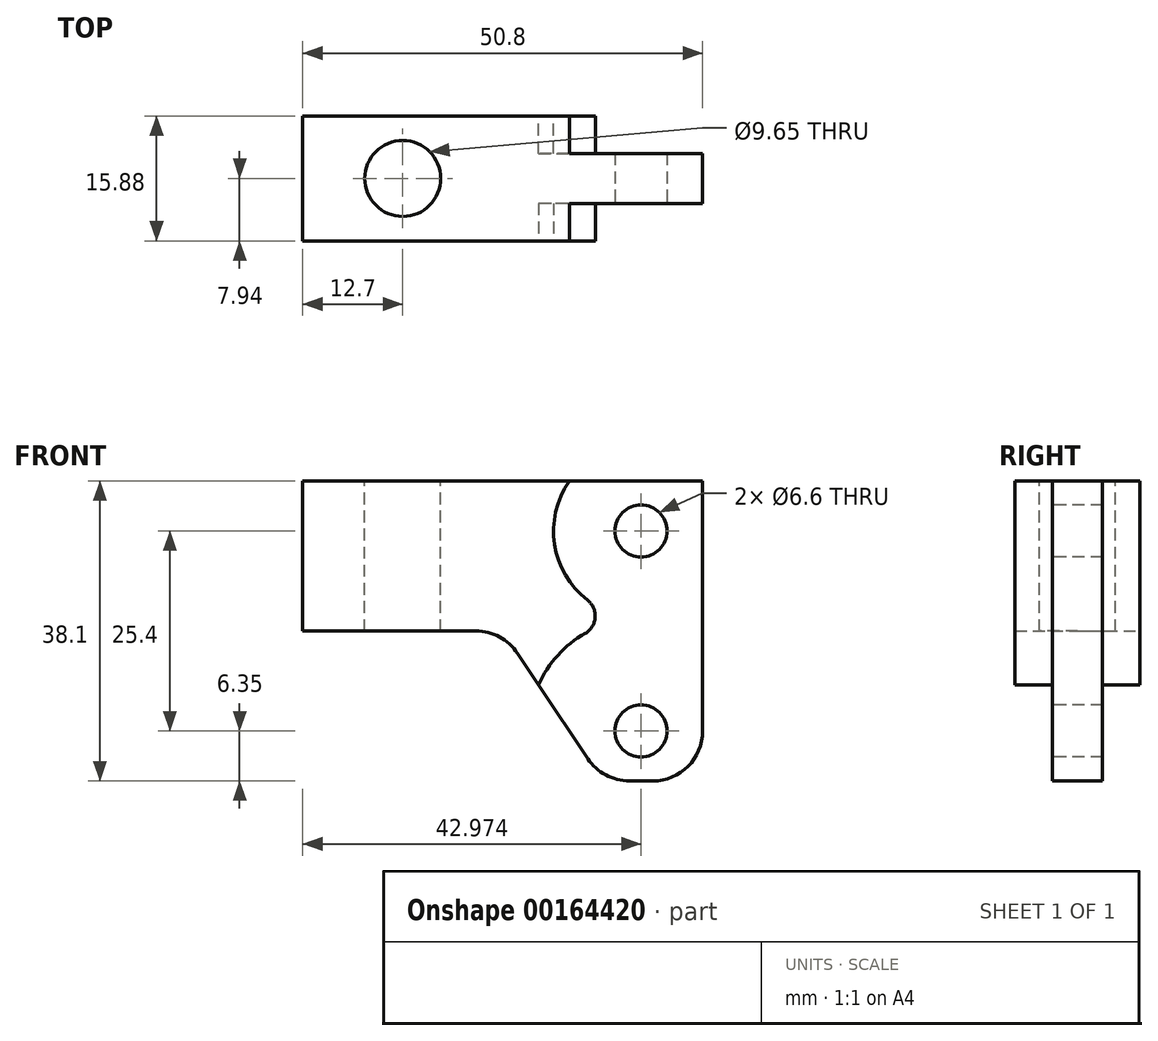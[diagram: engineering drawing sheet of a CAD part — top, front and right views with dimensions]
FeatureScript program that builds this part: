
annotation { "Feature Type Name" : "Feature", "Feature Type Description" : "" }
export const myFeature = defineFeature(function(context is Context, id is Id, definition is map)
    precondition{}
    {
        {
            var Q0;
            Q0=qCreatedBy(makeId("Front.planeOp"),FACE);
            var sketch = newSketch(context, id + "F0", { "sketchPlane" : qUnion([Q0])});
            skLineSegment(sketch, "E0", {"start": v(0, 0) * mm, "end": v(0, 19.05) * mm});
            skLineSegment(sketch, "E1", {"start": v(0, 19.05) * mm, "end": v(50.8, 19.05) * mm});
            skLineSegment(sketch, "E2", {"start": v(50.8, 19.05) * mm, "end": v(50.8, -19.05) * mm});
            skLineSegment(sketch, "E3", {"start": v(50.8, -19.05) * mm, "end": v(38.1, -19.05) * mm});
            skLineSegment(sketch, "E4", {"start": v(38.1, -19.05) * mm, "end": v(25.4, 0) * mm});
            skLineSegment(sketch, "E5", {"start": v(25.4, 0) * mm, "end": v(0, 0) * mm});
            skSolve(sketch);
        }
        {
            var Q0;
            Q0 = qSketchRegion(id + "F0", true);
            extrude(context, id + "F1", {"entities" : qUnion([Q0]), "depth" : 7.94 * mm, "hasSecondDirection" : true, "secondDirectionOppositeDirection" : true, "secondDirectionDepth" : 7.94 * mm});
        }
        {
            var Q0;
            Q0=makeQuery(id+"F1.opExtrude","SWEPT_EDGE",EDGE,{"disambiguationData":[OSD([sQuery(id+"F0.wireOp",EDGE,"E4"),sQuery(id+"F0.wireOp",EDGE,"E5")])]});
            var Q1;
            Q1=makeQuery(id+"F1.opExtrude","SWEPT_EDGE",EDGE,{"disambiguationData":[OSD([sQuery(id+"F0.wireOp",EDGE,"E3"),sQuery(id+"F0.wireOp",EDGE,"E4")])]});
            var Q2;
            Q2=makeQuery(id+"F1.opExtrude","SWEPT_EDGE",EDGE,{"disambiguationData":[OSD([sQuery(id+"F0.wireOp",EDGE,"E2"),sQuery(id+"F0.wireOp",EDGE,"E3")])]});
            fillet(context, id + "F2", {"entities" : qUnion([Q0, Q1, Q2]), "radius" : 6.35 * mm, "tangentPropagation" : true, "allowEdgeOverflow" : false});
        }
        {
            var Q0;
            Q0=makeQuery(id+"F1.opExtrude","CAP_FACE",FACE,{"disambiguationData":[OSD([sQuery(id+"F0.wireOp",EDGE,"E0"),sQuery(id+"F0.wireOp",EDGE,"E1"),sQuery(id+"F0.wireOp",EDGE,"E2"),sQuery(id+"F0.wireOp",EDGE,"E3"),sQuery(id+"F0.wireOp",EDGE,"E4"),sQuery(id+"F0.wireOp",EDGE,"E5")])],"isStart":false});
            var sketch = newSketch(context, id + "F3", { "sketchPlane" : qUnion([Q0])});
            skCircle(sketch, "E6", {"center": v(42.97, -12.7) * mm, "radius": 3.3 * mm});
            skCircle(sketch, "E7", {"center": v(42.97, 12.7) * mm, "radius": 3.3 * mm});
            skLineSegment(sketch, "E8", {"start": v(42.97, 12.7) * mm, "end": v(42.97, -12.7) * mm, "construction": true});
            skLineSegment(sketch, "E9", {"start": v(42.97, -12.7) * mm, "end": v(50.8, -12.7) * mm, "construction": true});
            skLineSegment(sketch, "E10", {"start": v(42.97, 12.7) * mm, "end": v(42.97, 19.05) * mm, "construction": true});
            skLineSegment(sketch, "E11", {"start": v(36.5, -8.94) * mm, "end": v(42.97, -18.65) * mm, "construction": true});
            skLineSegment(sketch, "E12", {"start": v(42.97, -12.7) * mm, "end": v(40.23, -14.53) * mm, "construction": true});
            skLineSegment(sketch, "E13", {"start": v(42.97, -12.7) * mm, "end": v(42.97, -19.05) * mm, "construction": true});
            skSolve(sketch);
        }
        {
            var Q0;
            Q0 = qSketchRegion(id + "F3", true);
            extrude(context, id + "F4", {"entities" : qUnion([Q0]), "operationType" : NewBodyOperationType.REMOVE, "oppositeDirection" : true, "depth" : 25.4 * mm});
        }
        {
            var Q0;
            Q0=makeQuery(id+"F1.opExtrude","CAP_FACE",FACE,{"disambiguationData":[OSD([sQuery(id+"F0.wireOp",EDGE,"E0"),sQuery(id+"F0.wireOp",EDGE,"E1"),sQuery(id+"F0.wireOp",EDGE,"E2"),sQuery(id+"F0.wireOp",EDGE,"E3"),sQuery(id+"F0.wireOp",EDGE,"E4"),sQuery(id+"F0.wireOp",EDGE,"E5")])],"isStart":false});
            var sketch = newSketch(context, id + "F5", { "sketchPlane" : qUnion([Q0])});
            skArc(sketch, "E14", {"start": v(42.97, 1.59) * mm, "mid": v(32.87, -22.8) * mm, "end": v(57.26, -12.7) * mm});
            skArc(sketch, "E15", {"start": v(54.09, 12.7) * mm, "mid": v(35.12, 20.56) * mm, "end": v(42.97, 1.59) * mm});
            skLineSegment(sketch, "E16.bottom", {"start": v(42.97, 12.7) * mm, "end": v(61.7, 12.7) * mm});
            skLineSegment(sketch, "E16.top", {"start": v(42.97, -12.7) * mm, "end": v(61.7, -12.7) * mm});
            skLineSegment(sketch, "E16.left", {"start": v(42.97, 12.7) * mm, "end": v(42.97, -12.7) * mm});
            skLineSegment(sketch, "E16.right", {"start": v(61.7, 12.7) * mm, "end": v(61.7, -12.7) * mm});
            skSolve(sketch);
        }
        {
            var Q0;
            Q0 = qSketchRegion(id + "F5", true);
            extrude(context, id + "F6", {"entities" : qUnion([Q0]), "operationType" : NewBodyOperationType.REMOVE, "oppositeDirection" : true, "depth" : 4.76 * mm});
        }
        {
            var Q0;
            Q0=makeQuery(id+"F6.boolean.opBoolean","COPY",EDGE,{"derivedFrom":makeQuery(id+"F6.opExtrude","SWEPT_EDGE",EDGE,{"disambiguationData":[OSD([sQuery(id+"F5.wireOp",EDGE,"E14"),sQuery(id+"F5.wireOp",EDGE,"E15")])]})});
            fillet(context, id + "F7", {"entities" : qUnion([Q0]), "radius" : 2.54 * mm, "tangentPropagation" : true, "allowEdgeOverflow" : false});
        }
        {
            var Q0;
            Q0=makeQuery(id+"F1.opExtrude","CAP_FACE",FACE,{"disambiguationData":[OSD([sQuery(id+"F0.wireOp",EDGE,"E0"),sQuery(id+"F0.wireOp",EDGE,"E1"),sQuery(id+"F0.wireOp",EDGE,"E2"),sQuery(id+"F0.wireOp",EDGE,"E3"),sQuery(id+"F0.wireOp",EDGE,"E4"),sQuery(id+"F0.wireOp",EDGE,"E5")])],"isStart":true});
            var sketch = newSketch(context, id + "F8", { "sketchPlane" : qUnion([Q0])});
            skArc(sketch, "E17.0", {"start": v(-50.8, -12.7) * mm, "mid": v(-48.94, -17.2) * mm, "end": v(-44.45, -19.05) * mm});
            skLineSegment(sketch, "E17.1", {"start": v(-50.8, 19.05) * mm, "end": v(-50.8, -12.7) * mm});
            skLineSegment(sketch, "E17.2", {"start": v(-44.45, -19.05) * mm, "end": v(-41.5, -19.05) * mm});
            skLineSegment(sketch, "E17.3", {"start": v(-33.85, 19.05) * mm, "end": v(-50.8, 19.05) * mm});
            skArc(sketch, "E17.4", {"start": v(-41.5, -19.05) * mm, "mid": v(-38.5, -18.3) * mm, "end": v(-36.21, -16.22) * mm});
            skArc(sketch, "E18.0", {"start": v(-35.88, -0.3) * mm, "mid": v(-32.4, -3.1) * mm, "end": v(-29.95, -6.83) * mm});
            skArc(sketch, "E18.1", {"start": v(-36.17, 3.91) * mm, "mid": v(-37.15, 1.73) * mm, "end": v(-35.88, -0.3) * mm});
            skArc(sketch, "E18.2", {"start": v(-33.85, 19.05) * mm, "mid": v(-31.99, 11.02) * mm, "end": v(-36.17, 3.91) * mm});
            skLineSegment(sketch, "E19", {"start": v(-36.21, -16.22) * mm, "end": v(-29.95, -6.83) * mm});
            skSolve(sketch);
        }
        {
            var Q0;
            Q0 = qSketchRegion(id + "F8", true);
            extrude(context, id + "F9", {"entities" : qUnion([Q0]), "operationType" : NewBodyOperationType.REMOVE, "oppositeDirection" : true, "depth" : 4.76 * mm});
        }
        {
            var Q0;
            Q0=makeQuery(id+"F1.opExtrude","SWEPT_FACE",FACE,{"disambiguationData":[OSD([sQuery(id+"F0.wireOp",EDGE,"E1")])]});
            var sketch = newSketch(context, id + "F10", { "sketchPlane" : qUnion([Q0])});
            skLineSegment(sketch, "E20", {"start": v(0, 0) * mm, "end": v(12.7, 0) * mm, "construction": true});
            skCircle(sketch, "E21", {"center": v(12.7, 0) * mm, "radius": 4.83 * mm});
            skSolve(sketch);
        }
        {
            var Q0;
            Q0 = qSketchRegion(id + "F10", true);
            extrude(context, id + "F11", {"entities" : qUnion([Q0]), "operationType" : NewBodyOperationType.REMOVE, "endBound" : BoundingType.THROUGH_ALL, "oppositeDirection" : true, "depth" : 25.4 * mm});
        }
    });
